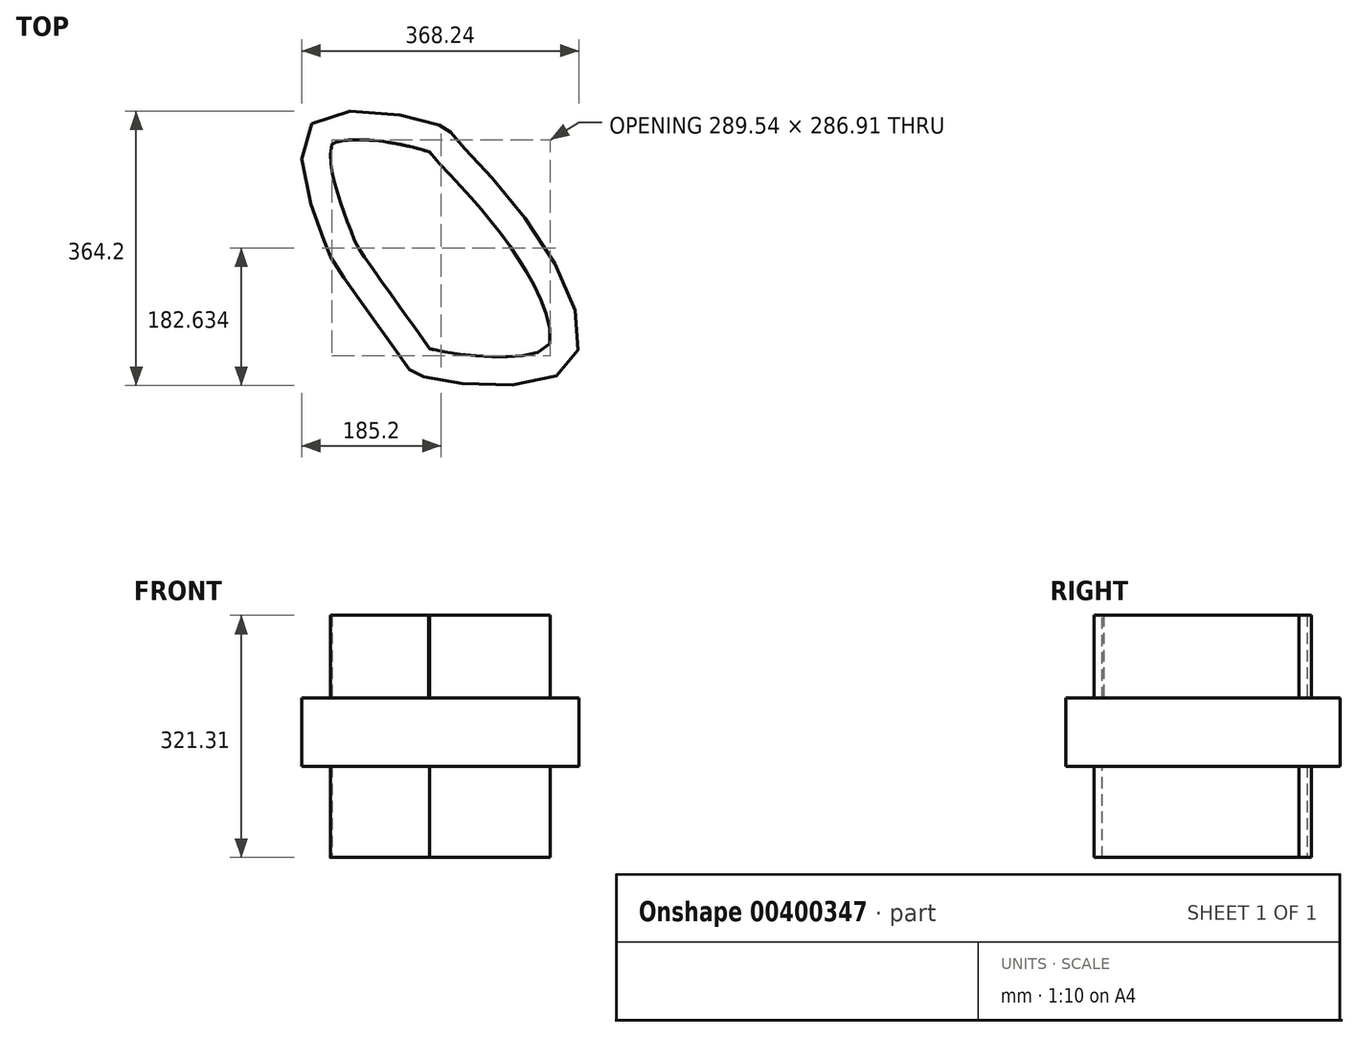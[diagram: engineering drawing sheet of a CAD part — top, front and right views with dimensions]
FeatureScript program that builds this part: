
annotation { "Feature Type Name" : "Feature", "Feature Type Description" : "" }
export const myFeature = defineFeature(function(context is Context, id is Id, definition is map)
    precondition{}
    {
        {
            var Q0;
            Q0=qCreatedBy(makeId("Top.planeOp"),FACE);
            var sketch = newSketch(context, id + "F0", { "sketchPlane" : qUnion([Q0])});
            skFitSpline(sketch, "E0", {"points": [v(-170.86, 148.3) * mm, v(-153.8, -8.77) * mm, v(-139.73, -38.83) * mm, v(-47.21, -169.79) * mm, v(-25.46, -186.68) * mm, v(165.41, -179.03) * mm, v(128.68, 0) * mm, v(14.48, 135.3) * mm, v(5.06, 144.05) * mm, v(-170.86, 148.3) * mm]});
            skSolve(sketch);
        }
        {
            var Q0;
            Q0=makeQuery(id+"F0.imprint","IMPRINT",FACE,{"disambiguationData":[TD([[makeQuery(id+"F0.imprint","IMPRINT",EDGE,{"derivedFrom":sQuery(id+"F0.wireOp",EDGE,"E0")}),1.0]])]});
            extrude(context, id + "F1", {"entities" : qUnion([Q0]), "depth" : 90.42 * mm});
        }
        {
            var Q0;
            Q0=makeQuery(id+"F1.opExtrude","CAP_FACE",FACE,{"disambiguationData":[OSD([sQuery(id+"F0.wireOp",EDGE,"E0")])],"isStart":false});
            shell(context, id + "F2", {"entities" : qUnion([Q0]), "thickness" : 38.1 * mm});
        }
        {
            var Q0;
            {var subQ0=sQuery(id+"F0.wireOp",EDGE,"E0");Q0=makeQuery(id+"F2.opShell","OFFSET_FACE",FACE,{"disambiguationData":[OSD([subQ0]),TDD([makeQuery(id+"F1.opExtrude","CAP_FACE",FACE,{"disambiguationData":[OSD([subQ0])],"isStart":true})])]});}
            extrude(context, id + "F3", {"entities" : qUnion([Q0]), "operationType" : NewBodyOperationType.ADD, "oppositeDirection" : true, "depth" : 159.26 * mm});
        }
        {
            var Q0;
            {var subQ0=sQuery(id+"F0.wireOp",EDGE,"E0");Q0=makeQuery(id+"F2.opShell","OFFSET_FACE",FACE,{"disambiguationData":[OSD([subQ0]),TDD([makeQuery(id+"F1.opExtrude","CAP_FACE",FACE,{"disambiguationData":[OSD([subQ0])],"isStart":true})])]});}
            extrude(context, id + "F4", {"entities" : qUnion([Q0]), "operationType" : NewBodyOperationType.ADD, "depth" : 162.05 * mm});
        }
    });
